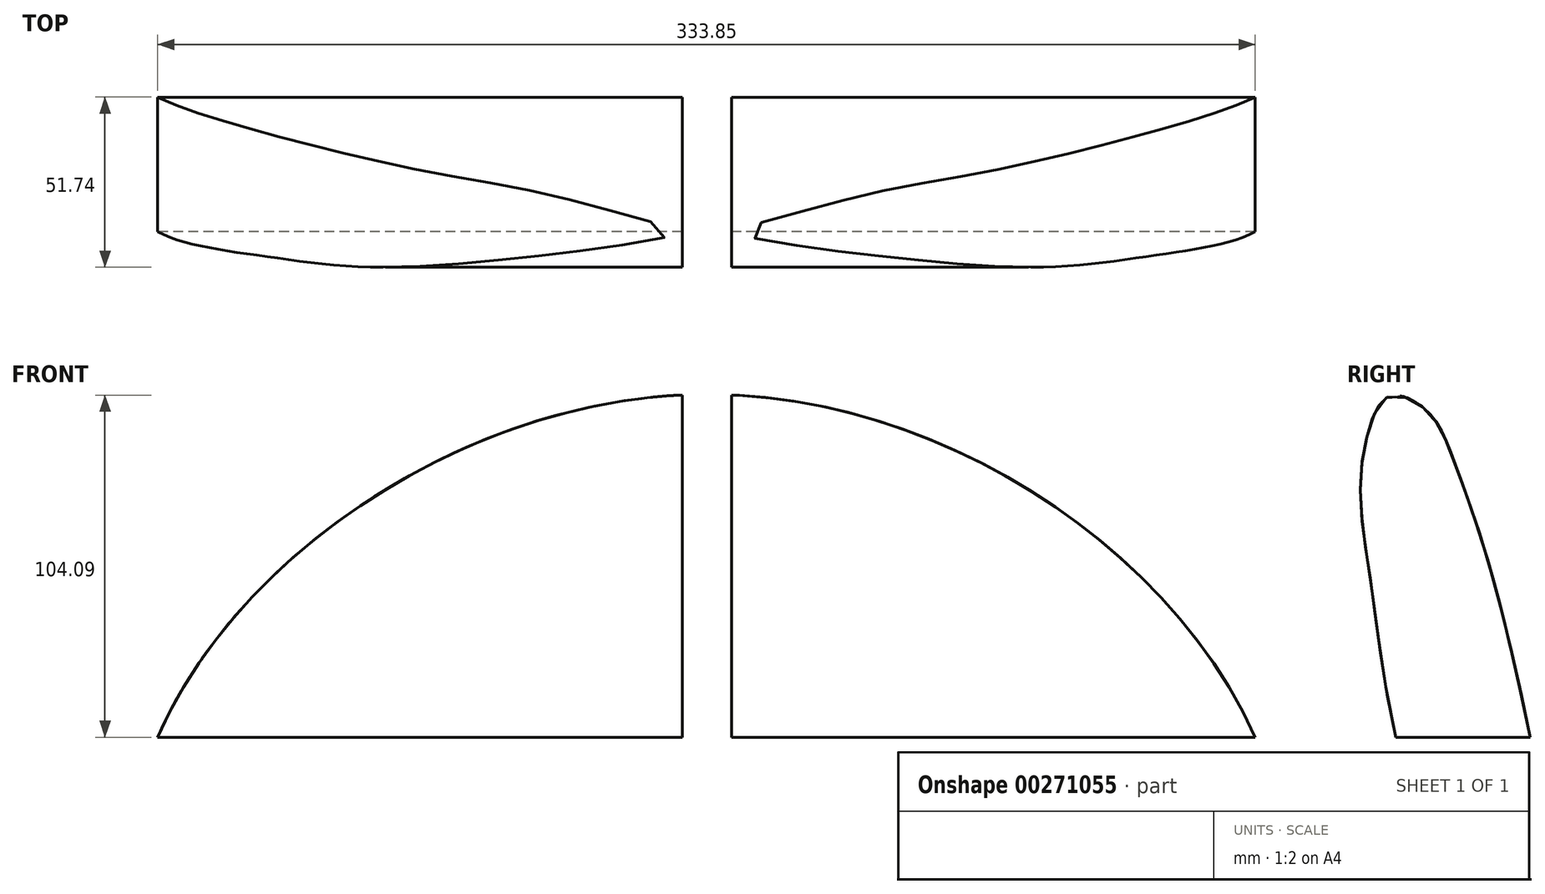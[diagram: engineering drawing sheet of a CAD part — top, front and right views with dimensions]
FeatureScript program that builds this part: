
annotation { "Feature Type Name" : "Feature", "Feature Type Description" : "" }
export const myFeature = defineFeature(function(context is Context, id is Id, definition is map)
    precondition{}
    {
        {
            var Q0;
            Q0=qCreatedBy(makeId("Front.planeOp"),FACE);
            var sketch = newSketch(context, id + "F0", { "sketchPlane" : qUnion([Q0])});
            skLineSegment(sketch, "E0", {"start": v(0, 0) * mm, "end": v(0, -120) * mm});
            skLineSegment(sketch, "E1", {"start": v(0, -120) * mm, "end": v(-172.5, -120) * mm});
            skLineSegment(sketch, "E2.MirrorCS", {"start": v(0, -120) * mm, "end": v(172.5, -120) * mm});
            skFitSpline(sketch, "E3", {"points": [v(-172.5, -120) * mm, v(0, 0) * mm, v(172.5, -120) * mm], "startDerivative": vector(101.52, 378.97) * mm, "endDerivative": vector(109.22, -382.9) * mm});
            skLineSegment(sketch, "E4", {"start": v(0, -120) * mm, "end": v(-7.5, -120) * mm});
            skLineSegment(sketch, "E5.MirrorCS", {"start": v(0, -120) * mm, "end": v(7.5, -120) * mm});
            skLineSegment(sketch, "E6", {"start": v(-7.5, -120) * mm, "end": v(-7.5, 1.37) * mm});
            skLineSegment(sketch, "E7", {"start": v(7.5, -120) * mm, "end": v(7.5, 6.88) * mm});
            skSolve(sketch);
        }
        {
            var Q0;
            {var subQ0=sQuery(id+"F0.wireOp",EDGE,"E1");Q0=makeQuery(id+"F0.imprint","IMPRINT",FACE,{"disambiguationData":[TD([[makeQuery(id+"F0.imprint","IMPRINT",EDGE,{"derivedFrom":subQ0}),-1.0]])]});}
            var Q1;
            {var subQ0=sQuery(id+"F0.wireOp",EDGE,"E2.MirrorCS");Q1=makeQuery(id+"F0.imprint","IMPRINT",FACE,{"disambiguationData":[TD([[makeQuery(id+"F0.imprint","IMPRINT",EDGE,{"derivedFrom":subQ0}),1.0]])]});}
            extrude(context, id + "F1", {"entities" : qUnion([Q0, Q1]), "depth" : 92 * mm});
        }
        {
            var Q0;
            Q0=makeQuery(id+"F1.opExtrude","SWEPT_FACE",FACE,{"disambiguationData":[OSD([sQuery(id+"F0.wireOp",EDGE,"E7")])]});
            var sketch = newSketch(context, id + "F2", { "sketchPlane" : qUnion([Q0])});
            skFitSpline(sketch, "E8", {"points": [v(70.88, -104.37) * mm, v(78.53, -56.52) * mm, v(81.61, -30.82) * mm, v(78.78, -9.74) * mm, v(72.16, -0.4) * mm, v(61.05, -5.37) * mm, v(54.1, -17.7) * mm, v(42.28, -52.4) * mm, v(29.88, -104.37) * mm], "startDerivative": vector(69.99, 299.65) * mm, "endDerivative": vector(-63.8, -297.22) * mm});
            skLineSegment(sketch, "E9", {"start": v(122.9, 18.04) * mm, "end": v(-8.91, 18.04) * mm});
            skLineSegment(sketch, "E10", {"start": v(-8.91, 18.04) * mm, "end": v(-8.91, -133.22) * mm});
            skLineSegment(sketch, "E11", {"start": v(-8.91, -133.22) * mm, "end": v(136.88, -133.22) * mm});
            skLineSegment(sketch, "E12", {"start": v(136.88, -133.22) * mm, "end": v(122.9, 18.04) * mm});
            skLineSegment(sketch, "E13", {"start": v(70.88, -104.37) * mm, "end": v(29.88, -104.37) * mm});
            skSolve(sketch);
        }
        {
            var Q0;
            Q0=makeQuery(id+"F2.imprint","IMPRINT",FACE,{"disambiguationData":[TD([[makeQuery(id+"F2.imprint","IMPRINT",EDGE,{"derivedFrom":sQuery(id+"F2.wireOp",EDGE,"E8")}),-1.0]])]});
            extrude(context, id + "F3", {"entities" : qUnion([Q0]), "operationType" : NewBodyOperationType.REMOVE, "endBound" : BoundingType.SYMMETRIC, "oppositeDirection" : true, "depth" : 460 * mm});
        }
        {
            var Q0;
            Q0 = qSketchRegion(id + "F2", true);
            extrude(context, id + "F4", {"entities" : qUnion([Q0]), "operationType" : NewBodyOperationType.REMOVE, "depth" : 334 * mm});
        }
    });
